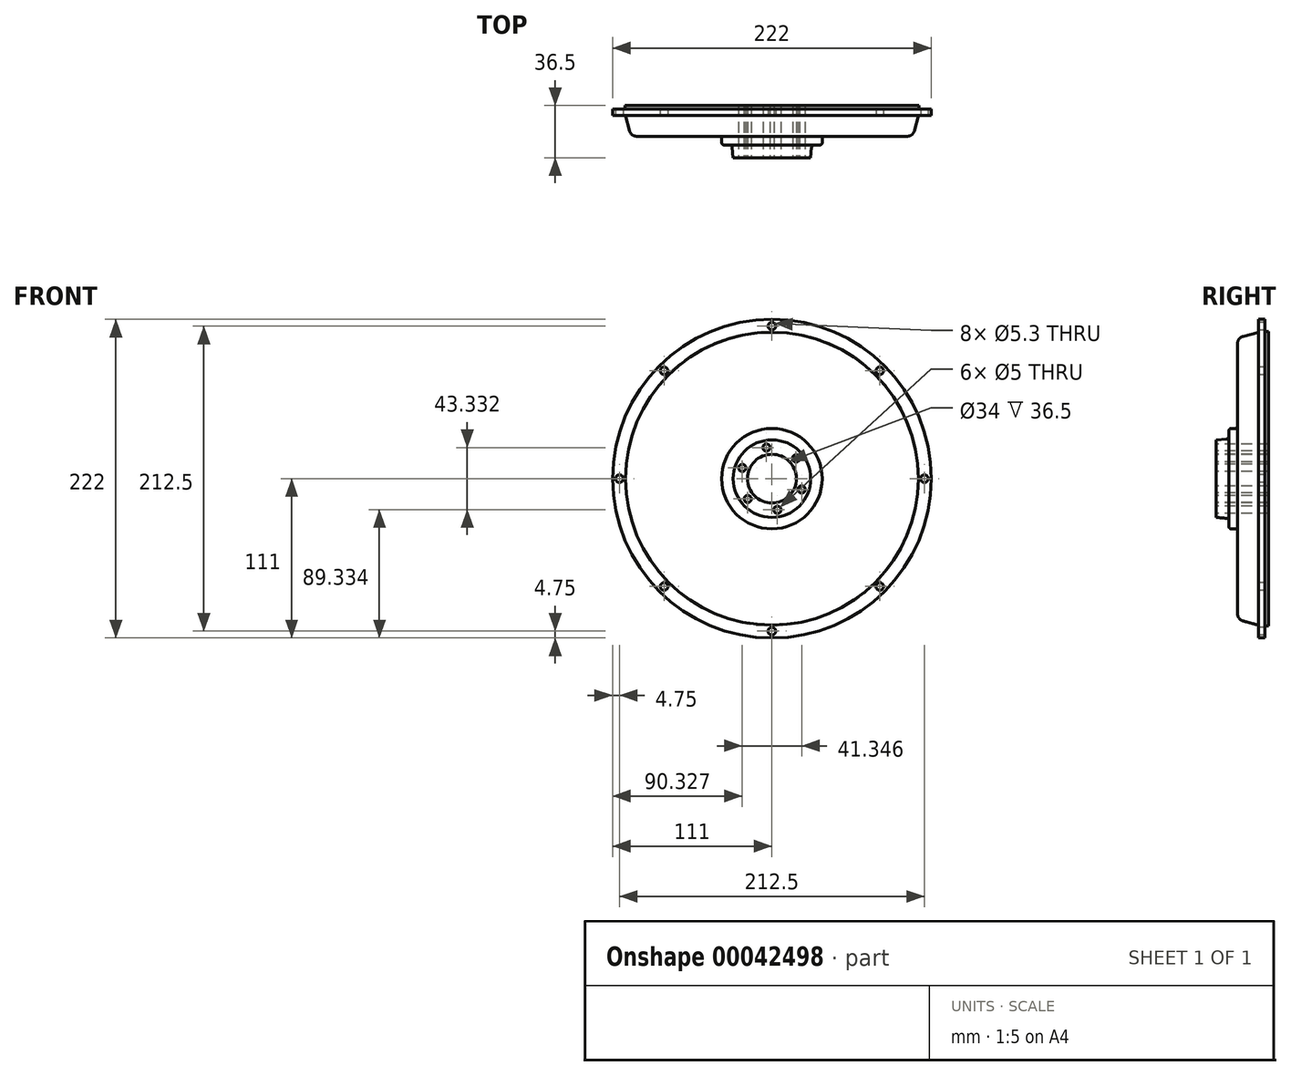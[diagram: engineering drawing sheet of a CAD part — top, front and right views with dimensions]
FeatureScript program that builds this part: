
annotation { "Feature Type Name" : "Feature", "Feature Type Description" : "" }
export const myFeature = defineFeature(function(context is Context, id is Id, definition is map)
    precondition{}
    {
        {
            var Q0;
            Q0=qCreatedBy(makeId("Right.planeOp"),FACE);
            var sketch = newSketch(context, id + "F0", { "sketchPlane" : qUnion([Q0])});
            skLineSegment(sketch, "E0", {"start": v(2.5, 102.5) * mm, "end": v(0, 102.5) * mm});
            skLineSegment(sketch, "E1", {"start": v(0, 102.5) * mm, "end": v(0, 111) * mm});
            skLineSegment(sketch, "E2", {"start": v(0, 111) * mm, "end": v(-4.6, 111) * mm});
            skLineSegment(sketch, "E3", {"start": v(-4.6, 111) * mm, "end": v(-4.6, 102) * mm});
            skLineSegment(sketch, "E4", {"start": v(-4.6, 102) * mm, "end": v(-15.3, 99.13) * mm});
            skLineSegment(sketch, "E5", {"start": v(-19, 94.3) * mm, "end": v(-19, 36.5) * mm});
            skLineSegment(sketch, "E6", {"start": v(-20.5, 35) * mm, "end": v(-23.5, 35) * mm});
            skLineSegment(sketch, "E7", {"start": v(-25, 33.5) * mm, "end": v(-25, 29.62) * mm});
            skLineSegment(sketch, "E8", {"start": v(-26.83, 27.63) * mm, "end": v(-34, 27) * mm});
            skLineSegment(sketch, "E9", {"start": v(-34, 27) * mm, "end": v(-34, 17) * mm});
            skLineSegment(sketch, "E10", {"start": v(-34, 17) * mm, "end": v(2.5, 17) * mm});
            skLineSegment(sketch, "E11", {"start": v(2.5, 17) * mm, "end": v(2.5, 102.5) * mm});
            skLineSegment(sketch, "E12", {"start": v(0, 0) * mm, "end": v(-52.31, 0) * mm, "construction": true});
            skPoint(sketch, "E13.visualSharp", {"position": v(-19, 98.14) * mm});
            skArc(sketch, "E13.filletArc", {"start": v(-15.3, 99.13) * mm, "mid": v(-17.97, 97.35) * mm, "end": v(-19, 94.3) * mm});
            skPoint(sketch, "E14.visualSharp", {"position": v(-25, 27.79) * mm});
            skArc(sketch, "E14.filletArc", {"start": v(-26.83, 27.63) * mm, "mid": v(-25.53, 28.27) * mm, "end": v(-25, 29.62) * mm});
            skPoint(sketch, "E15.visualSharp", {"position": v(-25, 35) * mm});
            skArc(sketch, "E15.filletArc", {"start": v(-23.5, 35) * mm, "mid": v(-24.56, 34.56) * mm, "end": v(-25, 33.5) * mm});
            skPoint(sketch, "E16.visualSharp", {"position": v(-19, 35) * mm});
            skArc(sketch, "E16.filletArc", {"start": v(-20.5, 35) * mm, "mid": v(-19.44, 35.44) * mm, "end": v(-19, 36.5) * mm});
            skSolve(sketch);
        }
        {
            var Q0;
            Q0 = qSketchRegion(id + "F0", true);
            var Q1;
            Q1=sQuery(id+"F0.wireOp",EDGE,"E12");
            revolve(context, id + "F1", {"entities" : qUnion([Q0]), "axis" : qUnion([Q1]), "revolveType" : RevolveType.FULL, "oppositeDirection" : true});
        }
        {
            var Q0;
            Q0=makeQuery(id+"F1.opRevolve","SWEPT_FACE",FACE,{"disambiguationData":[OSD([sQuery(id+"F0.wireOp",EDGE,"E3")])]});
            var sketch = newSketch(context, id + "F2", { "sketchPlane" : qUnion([Q0])});
            skCircle(sketch, "E17", {"center": v(-106.25, 0) * mm, "radius": 2.65 * mm});
            skCircle(sketch, "E18.1.0", {"center": v(-75.13, -75.13) * mm, "radius": 2.65 * mm});
            skCircle(sketch, "E18.2.0", {"center": v(0, -106.25) * mm, "radius": 2.65 * mm});
            skCircle(sketch, "E18.3.0", {"center": v(75.13, -75.13) * mm, "radius": 2.65 * mm});
            skCircle(sketch, "E18.4.0", {"center": v(106.25, 0) * mm, "radius": 2.65 * mm});
            skCircle(sketch, "E18.5.0", {"center": v(75.13, 75.13) * mm, "radius": 2.65 * mm});
            skCircle(sketch, "E18.6.0", {"center": v(0, 106.25) * mm, "radius": 2.65 * mm});
            skCircle(sketch, "E18.7.0", {"center": v(-75.13, 75.13) * mm, "radius": 2.65 * mm});
            skPoint(sketch, "E18.center", {"position": v(0, 0) * mm});
            skSolve(sketch);
        }
        {
            var Q0;
            Q0 = qSketchRegion(id + "F2", true);
            extrude(context, id + "F3", {"entities" : qUnion([Q0]), "operationType" : NewBodyOperationType.REMOVE, "endBound" : BoundingType.THROUGH_ALL, "oppositeDirection" : true, "depth" : 25 * mm});
        }
        {
            var Q0;
            Q0=makeQuery(id+"F1.opRevolve","SWEPT_FACE",FACE,{"disambiguationData":[OSD([sQuery(id+"F0.wireOp",EDGE,"E9")])]});
            var sketch = newSketch(context, id + "F4", { "sketchPlane" : qUnion([Q0])});
            skPoint(sketch, "E19", {"position": v(-3.82, 21.67) * mm});
            skPoint(sketch, "E20.1.0", {"position": v(-20.67, 7.52) * mm});
            skPoint(sketch, "E20.2.0", {"position": v(-16.85, -14.14) * mm});
            skPoint(sketch, "E20.3.0", {"position": v(3.82, -21.67) * mm});
            skPoint(sketch, "E20.4.0", {"position": v(20.67, -7.52) * mm});
            skPoint(sketch, "E20.5.0", {"position": v(16.85, 14.14) * mm});
            skPoint(sketch, "E20.center", {"position": v(0, 0) * mm});
            skLineSegment(sketch, "E21", {"start": v(0, 0) * mm, "end": v(0, 17) * mm, "construction": true});
            skLineSegment(sketch, "E22", {"start": v(0, 0) * mm, "end": v(-3.82, 21.67) * mm, "construction": true});
            skSolve(sketch);
        }
        {
            var Q0;
            Q0=sQuery(id+"F4.wireOp",VERTEX,"E19");
            var Q1;
            Q1=sQuery(id+"F4.wireOp",VERTEX,"E20.5.0");
            var Q2;
            Q2=sQuery(id+"F4.wireOp",VERTEX,"E20.4.0");
            var Q3;
            Q3=sQuery(id+"F4.wireOp",VERTEX,"E20.3.0");
            var Q4;
            Q4=sQuery(id+"F4.wireOp",VERTEX,"E20.2.0");
            var Q5;
            Q5=sQuery(id+"F4.wireOp",VERTEX,"E20.1.0");
            var Q6;
            Q6=makeQuery(id+"F1.opRevolve","SWEPT_BODY",BODY,{"disambiguationData":[OSD([sQuery(id+"F0.wireOp",EDGE,"E0"),sQuery(id+"F0.wireOp",EDGE,"E1"),sQuery(id+"F0.wireOp",EDGE,"E2"),sQuery(id+"F0.wireOp",EDGE,"E3"),sQuery(id+"F0.wireOp",EDGE,"E4"),sQuery(id+"F0.wireOp",EDGE,"E5"),sQuery(id+"F0.wireOp",EDGE,"E6"),sQuery(id+"F0.wireOp",EDGE,"E7"),sQuery(id+"F0.wireOp",EDGE,"E8"),sQuery(id+"F0.wireOp",EDGE,"E9"),sQuery(id+"F0.wireOp",EDGE,"E10"),sQuery(id+"F0.wireOp",EDGE,"E11"),sQuery(id+"F0.wireOp",EDGE,"E13.filletArc"),sQuery(id+"F0.wireOp",EDGE,"E14.filletArc"),sQuery(id+"F0.wireOp",EDGE,"E15.filletArc"),sQuery(id+"F0.wireOp",EDGE,"E16.filletArc")])]});
            hole(context, id + "F5", {"style" : HoleStyle.SIMPLE, "holeDiameter" : 5 * mm, "endStyle" : HoleEndStyle.THROUGH, "locations" : qUnion([Q0, Q1, Q2, Q3, Q4, Q5]), "scope" : qUnion([Q6])});
        }
    });
